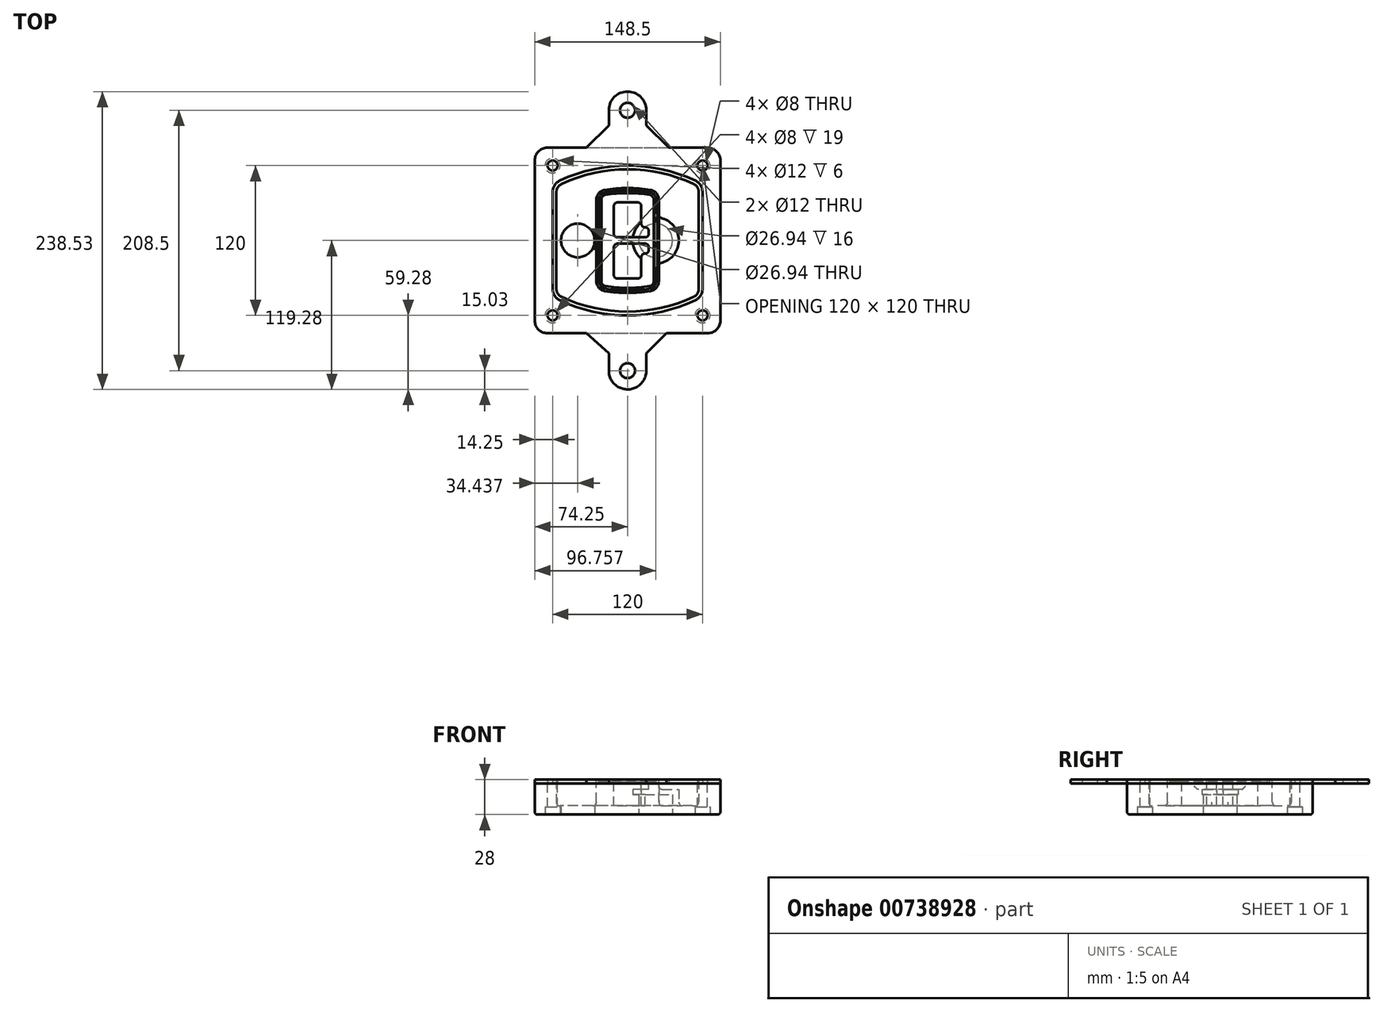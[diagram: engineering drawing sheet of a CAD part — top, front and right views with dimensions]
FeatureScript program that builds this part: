
annotation { "Feature Type Name" : "Feature", "Feature Type Description" : "" }
export const myFeature = defineFeature(function(context is Context, id is Id, definition is map)
    precondition{}
    {
        {
            var Q0;
            Q0=qCreatedBy(makeId("Top.planeOp"),FACE);
            var sketch = newSketch(context, id + "F0", { "sketchPlane" : qUnion([Q0])});
            skPoint(sketch, "E0.rect.middle", {"position": v(0, 0) * mm});
            skLineSegment(sketch, "E1.bottom", {"start": v(-64.25, -74.25) * mm, "end": v(64.25, -74.25) * mm});
            skLineSegment(sketch, "E1.top", {"start": v(-64.25, 74.25) * mm, "end": v(64.25, 74.25) * mm});
            skLineSegment(sketch, "E1.left", {"start": v(-74.25, -64.25) * mm, "end": v(-74.25, 64.25) * mm});
            skLineSegment(sketch, "E1.right", {"start": v(74.25, -64.25) * mm, "end": v(74.25, 64.25) * mm});
            skLineSegment(sketch, "E2", {"start": v(-74.25, 74.25) * mm, "end": v(74.25, -74.25) * mm, "construction": true});
            skLineSegment(sketch, "E3", {"start": v(74.25, 74.25) * mm, "end": v(-74.25, -74.25) * mm, "construction": true});
            skCircle(sketch, "E4", {"center": v(-60, 60) * mm, "radius": 4 * mm});
            skCircle(sketch, "E5", {"center": v(60, 60) * mm, "radius": 4 * mm});
            skCircle(sketch, "E6", {"center": v(60, -60) * mm, "radius": 4 * mm});
            skCircle(sketch, "E7", {"center": v(-60, -60) * mm, "radius": 4 * mm});
            skLineSegment(sketch, "E8", {"start": v(-60, 60) * mm, "end": v(60, 60) * mm, "construction": true});
            skLineSegment(sketch, "E9", {"start": v(60, 60) * mm, "end": v(60, -60) * mm, "construction": true});
            skLineSegment(sketch, "E10", {"start": v(60, -60) * mm, "end": v(-60, -60) * mm, "construction": true});
            skLineSegment(sketch, "E11", {"start": v(-60, -60) * mm, "end": v(-60, 60) * mm, "construction": true});
            skLineSegment(sketch, "E12", {"start": v(-60, 38.83) * mm, "end": v(-60, -38.83) * mm});
            skLineSegment(sketch, "E13", {"start": v(60, 38.83) * mm, "end": v(60, -38.83) * mm});
            skArc(sketch, "E14", {"start": v(54.26, 47.88) * mm, "mid": v(0, 60) * mm, "end": v(-54.26, 47.88) * mm});
            skArc(sketch, "E15", {"start": v(-54.26, -47.88) * mm, "mid": v(0, -60) * mm, "end": v(54.26, -47.88) * mm});
            skLineSegment(sketch, "E16", {"start": v(-60, 0) * mm, "end": v(60, 0) * mm, "construction": true});
            skPoint(sketch, "E17.visualSharp", {"position": v(-60, -45) * mm});
            skArc(sketch, "E17.filletArc", {"start": v(-60, -38.83) * mm, "mid": v(-58.44, -44.2) * mm, "end": v(-54.26, -47.88) * mm});
            skPoint(sketch, "E18.visualSharp", {"position": v(-60, 45) * mm});
            skArc(sketch, "E18.filletArc", {"start": v(-54.26, 47.88) * mm, "mid": v(-58.44, 44.2) * mm, "end": v(-60, 38.83) * mm});
            skPoint(sketch, "E19.visualSharp", {"position": v(60, 45) * mm});
            skArc(sketch, "E19.filletArc", {"start": v(60, 38.83) * mm, "mid": v(58.44, 44.2) * mm, "end": v(54.26, 47.88) * mm});
            skPoint(sketch, "E20.visualSharp", {"position": v(60, -45) * mm});
            skArc(sketch, "E20.filletArc", {"start": v(54.26, -47.88) * mm, "mid": v(58.44, -44.2) * mm, "end": v(60, -38.83) * mm});
            skPoint(sketch, "E21.visualSharp", {"position": v(-74.25, 74.25) * mm});
            skArc(sketch, "E21.filletArc", {"start": v(-64.25, 74.25) * mm, "mid": v(-71.32, 71.32) * mm, "end": v(-74.25, 64.25) * mm});
            skPoint(sketch, "E22.visualSharp", {"position": v(74.25, 74.25) * mm});
            skArc(sketch, "E22.filletArc", {"start": v(74.25, 64.25) * mm, "mid": v(71.32, 71.32) * mm, "end": v(64.25, 74.25) * mm});
            skPoint(sketch, "E23.visualSharp", {"position": v(74.25, -74.25) * mm});
            skArc(sketch, "E23.filletArc", {"start": v(64.25, -74.25) * mm, "mid": v(71.32, -71.32) * mm, "end": v(74.25, -64.25) * mm});
            skPoint(sketch, "E24.visualSharp", {"position": v(-74.25, -74.25) * mm});
            skArc(sketch, "E24.filletArc", {"start": v(-74.25, -64.25) * mm, "mid": v(-71.32, -71.32) * mm, "end": v(-64.25, -74.25) * mm});
            skArc(sketch, "E25.0", {"start": v(57, 38.83) * mm, "mid": v(55.9, 42.58) * mm, "end": v(52.98, 45.17) * mm});
            skLineSegment(sketch, "E25.1", {"start": v(57, 38.83) * mm, "end": v(57, -38.83) * mm});
            skArc(sketch, "E25.2", {"start": v(52.98, -45.17) * mm, "mid": v(55.9, -42.58) * mm, "end": v(57, -38.83) * mm});
            skArc(sketch, "E25.3", {"start": v(-52.98, -45.17) * mm, "mid": v(0, -57) * mm, "end": v(52.98, -45.17) * mm});
            skArc(sketch, "E25.4", {"start": v(-57, -38.83) * mm, "mid": v(-55.9, -42.58) * mm, "end": v(-52.98, -45.17) * mm});
            skArc(sketch, "E25.5", {"start": v(52.98, 45.17) * mm, "mid": v(0, 57) * mm, "end": v(-52.98, 45.17) * mm});
            skLineSegment(sketch, "E25.6", {"start": v(-57, 38.83) * mm, "end": v(-57, -38.83) * mm});
            skArc(sketch, "E25.7", {"start": v(-52.98, 45.17) * mm, "mid": v(-55.9, 42.58) * mm, "end": v(-57, 38.83) * mm});
            skArc(sketch, "E26.0", {"start": v(-55.96, 51.5) * mm, "mid": v(-61.82, 46.33) * mm, "end": v(-64, 38.83) * mm});
            skArc(sketch, "E26.1", {"start": v(55.96, 51.5) * mm, "mid": v(0, 64) * mm, "end": v(-55.96, 51.5) * mm});
            skArc(sketch, "E26.2", {"start": v(64, 38.83) * mm, "mid": v(61.82, 46.33) * mm, "end": v(55.96, 51.5) * mm});
            skLineSegment(sketch, "E26.3", {"start": v(64, 38.83) * mm, "end": v(64, -38.83) * mm});
            skArc(sketch, "E26.4", {"start": v(55.96, -51.5) * mm, "mid": v(61.82, -46.33) * mm, "end": v(64, -38.83) * mm});
            skLineSegment(sketch, "E26.5", {"start": v(-64, 38.83) * mm, "end": v(-64, -38.83) * mm});
            skArc(sketch, "E26.6", {"start": v(-55.96, -51.5) * mm, "mid": v(0, -64) * mm, "end": v(55.96, -51.5) * mm});
            skArc(sketch, "E26.7", {"start": v(-64, -38.83) * mm, "mid": v(-61.82, -46.33) * mm, "end": v(-55.96, -51.5) * mm});
            skSolve(sketch);
        }
        {
            var Q0;
            Q0=makeQuery(id+"F0.imprint","IMPRINT",FACE,{"disambiguationData":[TD([[makeQuery(id+"F0.imprint","IMPRINT",EDGE,{"derivedFrom":sQuery(id+"F0.wireOp",EDGE,"E1.bottom")}),1.0]])]});
            var Q1;
            Q1=makeQuery(id+"F0.imprint","IMPRINT",FACE,{"disambiguationData":[TD([[makeQuery(id+"F0.imprint","IMPRINT",EDGE,{"derivedFrom":sQuery(id+"F0.wireOp",EDGE,"E12")}),1.0]])]});
            var Q2;
            Q2=makeQuery(id+"F0.imprint","IMPRINT",FACE,{"disambiguationData":[TD([[makeQuery(id+"F0.imprint","IMPRINT",EDGE,{"derivedFrom":sQuery(id+"F0.wireOp",EDGE,"E25.0")}),1.0]])]});
            var Q3;
            Q3=makeQuery(id+"F0.imprint","IMPRINT",FACE,{"disambiguationData":[TD([[makeQuery(id+"F0.imprint","IMPRINT",EDGE,{"derivedFrom":sQuery(id+"F0.wireOp",EDGE,"E12")}),-1.0]])]});
            extrude(context, id + "F1", {"entities" : qUnion([Q0, Q1, Q2, Q3]), "oppositeDirection" : true, "depth" : 25 * mm, "offsetDistance" : 25 * mm});
        }
        {
            var Q0;
            Q0=makeQuery(id+"F0.imprint","IMPRINT",FACE,{"disambiguationData":[TD([[makeQuery(id+"F0.imprint","IMPRINT",EDGE,{"derivedFrom":sQuery(id+"F0.wireOp",EDGE,"E12")}),1.0]])]});
            extrude(context, id + "F2", {"entities" : qUnion([Q0]), "operationType" : NewBodyOperationType.ADD, "depth" : 3 * mm, "offsetDistance" : 25 * mm});
        }
        {
            var Q0;
            Q0=makeQuery(id+"F0.imprint","IMPRINT",FACE,{"disambiguationData":[TD([[makeQuery(id+"F0.imprint","IMPRINT",EDGE,{"derivedFrom":sQuery(id+"F0.wireOp",EDGE,"E25.0")}),1.0]])]});
            extrude(context, id + "F3", {"entities" : qUnion([Q0]), "operationType" : NewBodyOperationType.REMOVE, "oppositeDirection" : true, "depth" : 18 * mm});
        }
        {
            var Q0;
            Q0=makeQuery(id+"F2.opExtrude","CAP_FACE",FACE,{"disambiguationData":[OSD([sQuery(id+"F0.wireOp",EDGE,"E12"),sQuery(id+"F0.wireOp",EDGE,"E13"),sQuery(id+"F0.wireOp",EDGE,"E14"),sQuery(id+"F0.wireOp",EDGE,"E15"),sQuery(id+"F0.wireOp",EDGE,"E17.filletArc"),sQuery(id+"F0.wireOp",EDGE,"E18.filletArc"),sQuery(id+"F0.wireOp",EDGE,"E19.filletArc"),sQuery(id+"F0.wireOp",EDGE,"E20.filletArc"),sQuery(id+"F0.wireOp",EDGE,"E25.0"),sQuery(id+"F0.wireOp",EDGE,"E25.1"),sQuery(id+"F0.wireOp",EDGE,"E25.2"),sQuery(id+"F0.wireOp",EDGE,"E25.3"),sQuery(id+"F0.wireOp",EDGE,"E25.4"),sQuery(id+"F0.wireOp",EDGE,"E25.5"),sQuery(id+"F0.wireOp",EDGE,"E25.6"),sQuery(id+"F0.wireOp",EDGE,"E25.7")])],"isStart":false});
            var sketch = newSketch(context, id + "F4", { "sketchPlane" : qUnion([Q0])});
            skArc(sketch, "E27.0", {"start": v(-18.34, -40.45) * mm, "mid": v(0, -42) * mm, "end": v(18.34, -40.45) * mm});
            skArc(sketch, "E28.0", {"start": v(18.34, 40.45) * mm, "mid": v(0, 42) * mm, "end": v(-18.34, 40.45) * mm});
            skLineSegment(sketch, "E29", {"start": v(-25, 32.57) * mm, "end": v(-25, -32.57) * mm});
            skLineSegment(sketch, "E30", {"start": v(25, 32.57) * mm, "end": v(25, -32.57) * mm});
            skLineSegment(sketch, "E31", {"start": v(-25, 39.1) * mm, "end": v(25, 39.1) * mm, "construction": true});
            skLineSegment(sketch, "E32", {"start": v(-25, -39.1) * mm, "end": v(25, -39.1) * mm, "construction": true});
            skPoint(sketch, "E33.visualSharp", {"position": v(-25, 39.1) * mm});
            skArc(sketch, "E33.filletArc", {"start": v(-18.34, 40.45) * mm, "mid": v(-23.11, 37.73) * mm, "end": v(-25, 32.57) * mm});
            skPoint(sketch, "E34.visualSharp", {"position": v(25, 39.1) * mm});
            skArc(sketch, "E34.filletArc", {"start": v(25, 32.57) * mm, "mid": v(23.11, 37.73) * mm, "end": v(18.34, 40.45) * mm});
            skPoint(sketch, "E35.visualSharp", {"position": v(25, -39.1) * mm});
            skArc(sketch, "E35.filletArc", {"start": v(18.34, -40.45) * mm, "mid": v(23.11, -37.73) * mm, "end": v(25, -32.57) * mm});
            skPoint(sketch, "E36.visualSharp", {"position": v(-25, -39.1) * mm});
            skArc(sketch, "E36.filletArc", {"start": v(-25, -32.57) * mm, "mid": v(-23.11, -37.73) * mm, "end": v(-18.34, -40.45) * mm});
            skArc(sketch, "E37.0", {"start": v(52.98, 45.17) * mm, "mid": v(0, 57) * mm, "end": v(-52.98, 45.17) * mm});
            skArc(sketch, "E37.1", {"start": v(-52.98, 45.17) * mm, "mid": v(-55.9, 42.58) * mm, "end": v(-57, 38.83) * mm});
            skLineSegment(sketch, "E37.2", {"start": v(-57, 38.83) * mm, "end": v(-57, -38.83) * mm});
            skArc(sketch, "E37.3", {"start": v(-57, -38.83) * mm, "mid": v(-55.9, -42.58) * mm, "end": v(-52.98, -45.17) * mm});
            skArc(sketch, "E37.4", {"start": v(-52.98, -45.17) * mm, "mid": v(0, -57) * mm, "end": v(52.98, -45.17) * mm});
            skArc(sketch, "E37.5", {"start": v(52.98, -45.17) * mm, "mid": v(55.9, -42.58) * mm, "end": v(57, -38.83) * mm});
            skLineSegment(sketch, "E37.6", {"start": v(57, 38.83) * mm, "end": v(57, -38.83) * mm});
            skArc(sketch, "E37.7", {"start": v(57, 38.83) * mm, "mid": v(55.9, 42.58) * mm, "end": v(52.98, 45.17) * mm});
            skLineSegment(sketch, "E38.0", {"start": v(23, 32.57) * mm, "end": v(23, -32.57) * mm});
            skArc(sketch, "E38.1", {"start": v(18, -38.48) * mm, "mid": v(21.58, -36.44) * mm, "end": v(23, -32.57) * mm});
            skArc(sketch, "E38.2", {"start": v(-18, -38.48) * mm, "mid": v(0, -40) * mm, "end": v(18, -38.48) * mm});
            skArc(sketch, "E38.3", {"start": v(-23, -32.57) * mm, "mid": v(-21.58, -36.44) * mm, "end": v(-18, -38.48) * mm});
            skLineSegment(sketch, "E38.4", {"start": v(-23, 32.57) * mm, "end": v(-23, -32.57) * mm});
            skArc(sketch, "E38.5", {"start": v(23, 32.57) * mm, "mid": v(21.58, 36.44) * mm, "end": v(18, 38.48) * mm});
            skArc(sketch, "E38.6", {"start": v(-18, 38.48) * mm, "mid": v(-21.58, 36.44) * mm, "end": v(-23, 32.57) * mm});
            skArc(sketch, "E38.7", {"start": v(18, 38.48) * mm, "mid": v(0, 40) * mm, "end": v(-18, 38.48) * mm});
            skArc(sketch, "E39.0", {"start": v(21, 32.57) * mm, "mid": v(20.06, 35.15) * mm, "end": v(17.67, 36.5) * mm});
            skLineSegment(sketch, "E39.1", {"start": v(21, 32.57) * mm, "end": v(21, -32.57) * mm});
            skArc(sketch, "E39.2", {"start": v(17.67, -36.5) * mm, "mid": v(20.06, -35.15) * mm, "end": v(21, -32.57) * mm});
            skArc(sketch, "E39.3", {"start": v(-17.67, -36.5) * mm, "mid": v(0, -38) * mm, "end": v(17.67, -36.5) * mm});
            skArc(sketch, "E39.4", {"start": v(-21, -32.57) * mm, "mid": v(-20.06, -35.15) * mm, "end": v(-17.67, -36.5) * mm});
            skArc(sketch, "E39.5", {"start": v(17.67, 36.5) * mm, "mid": v(0, 38) * mm, "end": v(-17.67, 36.5) * mm});
            skLineSegment(sketch, "E39.6", {"start": v(-21, 32.57) * mm, "end": v(-21, -32.57) * mm});
            skArc(sketch, "E39.7", {"start": v(-17.67, 36.5) * mm, "mid": v(-20.06, 35.15) * mm, "end": v(-21, 32.57) * mm});
            skLineSegment(sketch, "E40", {"start": v(-25, 0) * mm, "end": v(25, 0) * mm, "construction": true});
            skLineSegment(sketch, "E41", {"start": v(-11, 5.5) * mm, "end": v(-11, 27.5) * mm});
            skLineSegment(sketch, "E42", {"start": v(-8, 30.5) * mm, "end": v(8, 30.5) * mm});
            skLineSegment(sketch, "E43", {"start": v(11, 27.5) * mm, "end": v(11, 13.5) * mm});
            skLineSegment(sketch, "E44", {"start": v(14, 10.5) * mm, "end": v(14, 10.5) * mm});
            skLineSegment(sketch, "E45", {"start": v(17, 7.5) * mm, "end": v(17, 5.5) * mm});
            skLineSegment(sketch, "E46", {"start": v(14, 2.5) * mm, "end": v(-8, 2.5) * mm});
            skPoint(sketch, "E47.visualSharp", {"position": v(-11, 30.5) * mm});
            skArc(sketch, "E47.filletArc", {"start": v(-8, 30.5) * mm, "mid": v(-10.12, 29.62) * mm, "end": v(-11, 27.5) * mm});
            skPoint(sketch, "E48.visualSharp", {"position": v(11, 30.5) * mm});
            skArc(sketch, "E48.filletArc", {"start": v(11, 27.5) * mm, "mid": v(10.12, 29.62) * mm, "end": v(8, 30.5) * mm});
            skPoint(sketch, "E49.visualSharp", {"position": v(11, 10.5) * mm});
            skArc(sketch, "E49.filletArc", {"start": v(11, 13.5) * mm, "mid": v(11.88, 11.38) * mm, "end": v(14, 10.5) * mm});
            skPoint(sketch, "E50.visualSharp", {"position": v(17, 10.5) * mm});
            skArc(sketch, "E50.filletArc", {"start": v(17, 7.5) * mm, "mid": v(16.12, 9.62) * mm, "end": v(14, 10.5) * mm});
            skPoint(sketch, "E51.visualSharp", {"position": v(17, 2.5) * mm});
            skArc(sketch, "E51.filletArc", {"start": v(14, 2.5) * mm, "mid": v(16.12, 3.38) * mm, "end": v(17, 5.5) * mm});
            skPoint(sketch, "E52.visualSharp", {"position": v(-11, 2.5) * mm});
            skArc(sketch, "E52.filletArc", {"start": v(-11, 5.5) * mm, "mid": v(-10.12, 3.38) * mm, "end": v(-8, 2.5) * mm});
            skLineSegment(sketch, "E53.0.MirrorCS", {"start": v(14, -2.5) * mm, "end": v(-8, -2.5) * mm});
            skArc(sketch, "E54.0.MirrorCS", {"start": v(-11, -5.5) * mm, "mid": v(-10.12, -3.38) * mm, "end": v(-8, -2.5) * mm});
            skLineSegment(sketch, "E55.0.MirrorCS", {"start": v(-11, -5.5) * mm, "end": v(-11, -27.5) * mm});
            skArc(sketch, "E56.0.MirrorCS", {"start": v(-8, -30.5) * mm, "mid": v(-10.12, -29.62) * mm, "end": v(-11, -27.5) * mm});
            skLineSegment(sketch, "E57.0.MirrorCS", {"start": v(-8, -30.5) * mm, "end": v(8, -30.5) * mm});
            skArc(sketch, "E58.0.MirrorCS", {"start": v(11, -27.5) * mm, "mid": v(10.12, -29.62) * mm, "end": v(8, -30.5) * mm});
            skLineSegment(sketch, "E59.0.MirrorCS", {"start": v(11, -27.5) * mm, "end": v(11, -13.5) * mm});
            skArc(sketch, "E60.0.MirrorCS", {"start": v(11, -13.5) * mm, "mid": v(11.88, -11.38) * mm, "end": v(14, -10.5) * mm});
            skArc(sketch, "E61.0.MirrorCS", {"start": v(17, -7.5) * mm, "mid": v(16.12, -9.62) * mm, "end": v(14, -10.5) * mm});
            skLineSegment(sketch, "E62.0.MirrorCS", {"start": v(17, -7.5) * mm, "end": v(17, -5.5) * mm});
            skArc(sketch, "E63.0.MirrorCS", {"start": v(14, -2.5) * mm, "mid": v(16.12, -3.38) * mm, "end": v(17, -5.5) * mm});
            skSolve(sketch);
        }
        {
            var Q0;
            Q0=makeQuery(id+"F4.imprint","IMPRINT",FACE,{"disambiguationData":[TD([[makeQuery(id+"F4.imprint","IMPRINT",EDGE,{"derivedFrom":sQuery(id+"F4.wireOp",EDGE,"E27.0")}),1.0]])]});
            var Q1;
            Q1=makeQuery(id+"F4.imprint","IMPRINT",FACE,{"disambiguationData":[TD([[makeQuery(id+"F4.imprint","IMPRINT",EDGE,{"derivedFrom":sQuery(id+"F4.wireOp",EDGE,"E38.0")}),-1.0]])]});
            var Q2;
            Q2=makeQuery(id+"F4.imprint","IMPRINT",FACE,{"disambiguationData":[TD([[makeQuery(id+"F4.imprint","IMPRINT",EDGE,{"derivedFrom":sQuery(id+"F4.wireOp",EDGE,"E39.0")}),1.0]])]});
            extrude(context, id + "F5", {"entities" : qUnion([Q0, Q1, Q2]), "operationType" : NewBodyOperationType.ADD, "endBound" : BoundingType.UP_TO_NEXT, "oppositeDirection" : true, "depth" : 25 * mm});
        }
        {
            var Q0;
            Q0=makeQuery(id+"F4.imprint","IMPRINT",FACE,{"disambiguationData":[TD([[makeQuery(id+"F4.imprint","IMPRINT",EDGE,{"derivedFrom":sQuery(id+"F4.wireOp",EDGE,"E38.0")}),-1.0]])]});
            extrude(context, id + "F6", {"entities" : qUnion([Q0]), "operationType" : NewBodyOperationType.REMOVE, "oppositeDirection" : true, "depth" : 2 * mm});
        }
        {
            var Q0;
            Q0=makeQuery(id+"F1.opExtrude","CAP_FACE",FACE,{"disambiguationData":[OSD([sQuery(id+"F0.wireOp",EDGE,"E1.bottom"),sQuery(id+"F0.wireOp",EDGE,"E1.top"),sQuery(id+"F0.wireOp",EDGE,"E1.left"),sQuery(id+"F0.wireOp",EDGE,"E1.right"),sQuery(id+"F0.wireOp",EDGE,"E4"),sQuery(id+"F0.wireOp",EDGE,"E5"),sQuery(id+"F0.wireOp",EDGE,"E6"),sQuery(id+"F0.wireOp",EDGE,"E7"),sQuery(id+"F0.wireOp",EDGE,"E21.filletArc"),sQuery(id+"F0.wireOp",EDGE,"E22.filletArc"),sQuery(id+"F0.wireOp",EDGE,"E23.filletArc"),sQuery(id+"F0.wireOp",EDGE,"E24.filletArc")])],"isStart":false});
            var sketch = newSketch(context, id + "F7", { "sketchPlane" : qUnion([Q0])});
            skCircle(sketch, "E64", {"center": v(22.5, 0) * mm, "radius": 13.47 * mm});
            skCircle(sketch, "E65", {"center": v(-39.81, 0) * mm, "radius": 13.47 * mm});
            skLineSegment(sketch, "E66", {"start": v(74.25, 0) * mm, "end": v(-74.25, 0) * mm});
            skCircle(sketch, "E67", {"center": v(22.5, 0) * mm, "radius": 18.47 * mm});
            skCircle(sketch, "E68", {"center": v(60, -60) * mm, "radius": 6 * mm});
            skCircle(sketch, "E69", {"center": v(-60, -60) * mm, "radius": 6 * mm});
            skCircle(sketch, "E70", {"center": v(-60, 60) * mm, "radius": 6 * mm});
            skCircle(sketch, "E71", {"center": v(60, 60) * mm, "radius": 6 * mm});
            skSolve(sketch);
        }
        {
            var Q0;
            {var subQ1=sQuery(id+"F7.wireOp",EDGE,"E66");var subQ4=sQuery(id+"F7.wireOp",EDGE,"E64");var subQ6=makeQuery(id+"F7.imprint","INTERSECT",VERTEX,{"disambiguationData":[OD(0.0)],"derivedFrom":[subQ4,subQ1]});Q0=makeQuery(id+"F7.imprint","IMPRINT",FACE,{"disambiguationData":[TD([[makeQuery(id+"F7.imprint","IMPRINT",EDGE,{"disambiguationData":[TD([[subQ6,-1.0]])],"derivedFrom":subQ4}),-1.0]])]});}
            var Q1;
            {var subQ0=sQuery(id+"F7.wireOp",EDGE,"E66");var subQ1=sQuery(id+"F7.wireOp",EDGE,"E64");var subQ3=makeQuery(id+"F7.imprint","INTERSECT",VERTEX,{"disambiguationData":[OD(0.0)],"derivedFrom":[subQ1,subQ0]});Q1=makeQuery(id+"F7.imprint","IMPRINT",FACE,{"disambiguationData":[TD([[makeQuery(id+"F7.imprint","IMPRINT",EDGE,{"disambiguationData":[TD([[subQ3,-1.0]])],"derivedFrom":subQ1}),1.0]])]});}
            var Q2;
            {var subQ0=sQuery(id+"F7.wireOp",EDGE,"E66");var subQ1=sQuery(id+"F7.wireOp",EDGE,"E64");var subQ3=makeQuery(id+"F7.imprint","INTERSECT",VERTEX,{"disambiguationData":[OD(0.0)],"derivedFrom":[subQ1,subQ0]});Q2=makeQuery(id+"F7.imprint","IMPRINT",FACE,{"disambiguationData":[TD([[makeQuery(id+"F7.imprint","IMPRINT",EDGE,{"disambiguationData":[TD([[subQ3,1.0]])],"derivedFrom":subQ1}),1.0]])]});}
            var Q3;
            {var subQ1=sQuery(id+"F7.wireOp",EDGE,"E66");var subQ4=sQuery(id+"F7.wireOp",EDGE,"E64");var subQ6=makeQuery(id+"F7.imprint","INTERSECT",VERTEX,{"disambiguationData":[OD(0.0)],"derivedFrom":[subQ4,subQ1]});Q3=makeQuery(id+"F7.imprint","IMPRINT",FACE,{"disambiguationData":[TD([[makeQuery(id+"F7.imprint","IMPRINT",EDGE,{"disambiguationData":[TD([[subQ6,1.0]])],"derivedFrom":subQ4}),-1.0]])]});}
            extrude(context, id + "F8", {"entities" : qUnion([Q0, Q1, Q2, Q3]), "operationType" : NewBodyOperationType.ADD, "oppositeDirection" : true, "depth" : 20 * mm});
        }
        {
            var Q0;
            {var subQ0=sQuery(id+"F7.wireOp",EDGE,"E66");var subQ1=sQuery(id+"F7.wireOp",EDGE,"E64");var subQ3=makeQuery(id+"F7.imprint","INTERSECT",VERTEX,{"disambiguationData":[OD(0.0)],"derivedFrom":[subQ1,subQ0]});Q0=makeQuery(id+"F7.imprint","IMPRINT",FACE,{"disambiguationData":[TD([[makeQuery(id+"F7.imprint","IMPRINT",EDGE,{"disambiguationData":[TD([[subQ3,-1.0]])],"derivedFrom":subQ1}),1.0]])]});}
            var Q1;
            {var subQ0=sQuery(id+"F7.wireOp",EDGE,"E66");var subQ1=sQuery(id+"F7.wireOp",EDGE,"E64");var subQ3=makeQuery(id+"F7.imprint","INTERSECT",VERTEX,{"disambiguationData":[OD(0.0)],"derivedFrom":[subQ1,subQ0]});Q1=makeQuery(id+"F7.imprint","IMPRINT",FACE,{"disambiguationData":[TD([[makeQuery(id+"F7.imprint","IMPRINT",EDGE,{"disambiguationData":[TD([[subQ3,1.0]])],"derivedFrom":subQ1}),1.0]])]});}
            extrude(context, id + "F9", {"entities" : qUnion([Q0, Q1]), "operationType" : NewBodyOperationType.REMOVE, "oppositeDirection" : true, "depth" : 16 * mm});
        }
        {
            var Q0;
            {var subQ0=sQuery(id+"F7.wireOp",EDGE,"E66");var subQ1=sQuery(id+"F7.wireOp",EDGE,"E65");var subQ3=makeQuery(id+"F7.imprint","INTERSECT",VERTEX,{"disambiguationData":[OD(0.0)],"derivedFrom":[subQ1,subQ0]});Q0=makeQuery(id+"F7.imprint","IMPRINT",FACE,{"disambiguationData":[TD([[makeQuery(id+"F7.imprint","IMPRINT",EDGE,{"disambiguationData":[TD([[subQ3,-1.0]])],"derivedFrom":subQ1}),1.0]])]});}
            var Q1;
            {var subQ0=sQuery(id+"F7.wireOp",EDGE,"E66");var subQ1=sQuery(id+"F7.wireOp",EDGE,"E65");var subQ3=makeQuery(id+"F7.imprint","INTERSECT",VERTEX,{"disambiguationData":[OD(0.0)],"derivedFrom":[subQ1,subQ0]});Q1=makeQuery(id+"F7.imprint","IMPRINT",FACE,{"disambiguationData":[TD([[makeQuery(id+"F7.imprint","IMPRINT",EDGE,{"disambiguationData":[TD([[subQ3,1.0]])],"derivedFrom":subQ1}),1.0]])]});}
            extrude(context, id + "F10", {"entities" : qUnion([Q0, Q1]), "operationType" : NewBodyOperationType.REMOVE, "oppositeDirection" : true, "depth" : 25 * mm});
        }
        {
            var Q0;
            Q0=makeQuery(id+"F7.imprint","IMPRINT",FACE,{"disambiguationData":[TD([[makeQuery(id+"F7.imprint","IMPRINT",EDGE,{"derivedFrom":sQuery(id+"F7.wireOp",EDGE,"E68")}),1.0]])]});
            var Q1;
            Q1=makeQuery(id+"F7.imprint","IMPRINT",FACE,{"disambiguationData":[TD([[makeQuery(id+"F7.imprint","IMPRINT",EDGE,{"derivedFrom":makeQuery(id+"F1.opExtrude","CAP_EDGE",EDGE,{"disambiguationData":[OSD([sQuery(id+"F0.wireOp",EDGE,"E5")])],"isStart":false})}),-1.0]])]});
            var Q2;
            Q2=makeQuery(id+"F7.imprint","IMPRINT",FACE,{"disambiguationData":[TD([[makeQuery(id+"F7.imprint","IMPRINT",EDGE,{"derivedFrom":sQuery(id+"F7.wireOp",EDGE,"E69")}),1.0]])]});
            var Q3;
            Q3=makeQuery(id+"F7.imprint","IMPRINT",FACE,{"disambiguationData":[TD([[makeQuery(id+"F7.imprint","IMPRINT",EDGE,{"derivedFrom":makeQuery(id+"F1.opExtrude","CAP_EDGE",EDGE,{"disambiguationData":[OSD([sQuery(id+"F0.wireOp",EDGE,"E4")])],"isStart":false})}),-1.0]])]});
            var Q4;
            Q4=makeQuery(id+"F7.imprint","IMPRINT",FACE,{"disambiguationData":[TD([[makeQuery(id+"F7.imprint","IMPRINT",EDGE,{"derivedFrom":sQuery(id+"F7.wireOp",EDGE,"E70")}),1.0]])]});
            var Q5;
            Q5=makeQuery(id+"F7.imprint","IMPRINT",FACE,{"disambiguationData":[TD([[makeQuery(id+"F7.imprint","IMPRINT",EDGE,{"derivedFrom":makeQuery(id+"F1.opExtrude","CAP_EDGE",EDGE,{"disambiguationData":[OSD([sQuery(id+"F0.wireOp",EDGE,"E7")])],"isStart":false})}),-1.0]])]});
            var Q6;
            Q6=makeQuery(id+"F7.imprint","IMPRINT",FACE,{"disambiguationData":[TD([[makeQuery(id+"F7.imprint","IMPRINT",EDGE,{"derivedFrom":sQuery(id+"F7.wireOp",EDGE,"E71")}),1.0]])]});
            var Q7;
            Q7=makeQuery(id+"F7.imprint","IMPRINT",FACE,{"disambiguationData":[TD([[makeQuery(id+"F7.imprint","IMPRINT",EDGE,{"derivedFrom":makeQuery(id+"F1.opExtrude","CAP_EDGE",EDGE,{"disambiguationData":[OSD([sQuery(id+"F0.wireOp",EDGE,"E6")])],"isStart":false})}),-1.0]])]});
            extrude(context, id + "F11", {"entities" : qUnion([Q0, Q1, Q2, Q3, Q4, Q5, Q6, Q7]), "operationType" : NewBodyOperationType.REMOVE, "oppositeDirection" : true, "depth" : 6 * mm});
        }
        {
            var Q0;
            Q0=makeQuery(id+"F9.boolean.opBoolean","COPY",FACE,{"derivedFrom":makeQuery(id+"F9.opExtrude","CAP_FACE",FACE,{"disambiguationData":[OSD([sQuery(id+"F7.wireOp",EDGE,"E64")])],"isStart":false})});
            var sketch = newSketch(context, id + "F12", { "sketchPlane" : qUnion([Q0])});
            skArc(sketch, "E72.0", {"start": v(11, 14.45) * mm, "mid": v(6.45, 9.13) * mm, "end": v(4.2, 2.5) * mm});
            skArc(sketch, "E72.1", {"start": v(4.2, -2.5) * mm, "mid": v(6.45, -9.13) * mm, "end": v(11, -14.45) * mm});
            skLineSegment(sketch, "E73", {"start": v(4.2, -2.5) * mm, "end": v(14, -2.5) * mm});
            skLineSegment(sketch, "E74.0", {"start": v(14, 2.5) * mm, "end": v(4.2, 2.5) * mm});
            skArc(sketch, "E74.1", {"start": v(14, 2.5) * mm, "mid": v(16.12, 3.38) * mm, "end": v(17, 5.5) * mm});
            skLineSegment(sketch, "E74.2", {"start": v(17, 7.5) * mm, "end": v(17, 5.5) * mm});
            skArc(sketch, "E74.3", {"start": v(17, 7.5) * mm, "mid": v(16.12, 9.62) * mm, "end": v(14, 10.5) * mm});
            skArc(sketch, "E74.4", {"start": v(11, 13.5) * mm, "mid": v(11.88, 11.38) * mm, "end": v(14, 10.5) * mm});
            skLineSegment(sketch, "E74.5", {"start": v(11, 14.45) * mm, "end": v(11, 13.5) * mm});
            skLineSegment(sketch, "E74.7", {"start": v(14, -2.5) * mm, "end": v(4.2, -2.5) * mm});
            skArc(sketch, "E74.8", {"start": v(14, -2.5) * mm, "mid": v(16.12, -3.38) * mm, "end": v(17, -5.5) * mm});
            skLineSegment(sketch, "E74.9", {"start": v(17, -7.5) * mm, "end": v(17, -5.5) * mm});
            skArc(sketch, "E74.10", {"start": v(17, -7.5) * mm, "mid": v(16.12, -9.62) * mm, "end": v(14, -10.5) * mm});
            skArc(sketch, "E74.11", {"start": v(11, -13.5) * mm, "mid": v(11.88, -11.38) * mm, "end": v(14, -10.5) * mm});
            skLineSegment(sketch, "E74.12", {"start": v(11, -14.45) * mm, "end": v(11, -13.5) * mm});
            skPoint(sketch, "E75.orphan", {"position": v(11, -27.5) * mm});
            skPoint(sketch, "E76.orphan", {"position": v(-8, -2.5) * mm});
            skPoint(sketch, "E77.orphan", {"position": v(-8, 2.5) * mm});
            skPoint(sketch, "E78.orphan", {"position": v(11, 27.5) * mm});
            skSolve(sketch);
        }
        {
            var Q0;
            {var subQ7=sQuery(id+"F12.wireOp",EDGE,"E72.0");var subQ14=sQuery(id+"F12.wireOp",EDGE,"E72.1");var subQ16=sQuery(id+"F12.wireOp",EDGE,"E74.1");var subQ18=sQuery(id+"F12.wireOp",EDGE,"E74.8");Q0=qUnion([makeQuery(id+"F12.imprint","IMPRINT",FACE,{"disambiguationData":[TD([[makeQuery(id+"F12.imprint","IMPRINT",EDGE,{"derivedFrom":subQ7}),1.0]])]}),makeQuery(id+"F12.imprint","IMPRINT",FACE,{"disambiguationData":[TD([[makeQuery(id+"F12.imprint","IMPRINT",EDGE,{"derivedFrom":subQ14}),1.0]])]}),makeQuery(id+"F12.imprint","IMPRINT",FACE,{"disambiguationData":[TD([[makeQuery(id+"F12.imprint","IMPRINT",EDGE,{"derivedFrom":subQ16}),1.0]])]}),makeQuery(id+"F12.imprint","IMPRINT",FACE,{"disambiguationData":[TD([[makeQuery(id+"F12.imprint","IMPRINT",EDGE,{"derivedFrom":subQ18}),-1.0]])]})]);}
            var Q1;
            Q1=makeQuery(id+"F5.boolean.opBoolean","SPLIT",FACE,{"disambiguationData":[TD([makeQuery(id+"F5.opExtrude","SWEPT_FACE",FACE,{"disambiguationData":[OSD([sQuery(id+"F4.wireOp",EDGE,"E41")])]})])],"derivedFrom":makeQuery(id+"F3.boolean.opBoolean","COPY",FACE,{"derivedFrom":makeQuery(id+"F3.opExtrude","CAP_FACE",FACE,{"disambiguationData":[OSD([sQuery(id+"F0.wireOp",EDGE,"E25.0"),sQuery(id+"F0.wireOp",EDGE,"E25.1"),sQuery(id+"F0.wireOp",EDGE,"E25.2"),sQuery(id+"F0.wireOp",EDGE,"E25.3"),sQuery(id+"F0.wireOp",EDGE,"E25.4"),sQuery(id+"F0.wireOp",EDGE,"E25.5"),sQuery(id+"F0.wireOp",EDGE,"E25.6"),sQuery(id+"F0.wireOp",EDGE,"E25.7")])],"isStart":false})})});
            extrude(context, id + "F13", {"entities" : qUnion([Q0]), "operationType" : NewBodyOperationType.REMOVE, "endBound" : BoundingType.UP_TO_SURFACE, "endBoundEntityFace" : qUnion([Q1]), "depth" : 25 * mm});
        }
        {
            var Q0;
            Q0=makeQuery(id+"F3.boolean.opBoolean","COPY",EDGE,{"derivedFrom":makeQuery(id+"F3.opExtrude","CAP_EDGE",EDGE,{"disambiguationData":[OSD([sQuery(id+"F0.wireOp",EDGE,"E25.6")])],"isStart":false})});
            var Q1;
            Q1=makeQuery(id+"F8.boolean.opBoolean","INTERSECT",EDGE,{"derivedFrom":[makeQuery(id+"F5.opExtrude","SWEPT_FACE",FACE,{"disambiguationData":[OSD([sQuery(id+"F4.wireOp",EDGE,"E30")])]}),makeQuery(id+"F8.opExtrude","CAP_FACE",FACE,{"disambiguationData":[OSD([sQuery(id+"F7.wireOp",EDGE,"E67")])],"isStart":false})]});
            var Q2;
            Q2=makeQuery(id+"F8.boolean.opBoolean","INTERSECT",EDGE,{"disambiguationData":[OD(1.0)],"derivedFrom":[makeQuery(id+"F5.opExtrude","SWEPT_FACE",FACE,{"disambiguationData":[OSD([sQuery(id+"F4.wireOp",EDGE,"E30")])]}),makeQuery(id+"F8.opExtrude","SWEPT_FACE",FACE,{"disambiguationData":[OSD([sQuery(id+"F7.wireOp",EDGE,"E67")])]})]});
            var Q3;
            {var subQ0=sQuery(id+"F4.wireOp",EDGE,"E30");Q3=makeQuery(id+"F8.boolean.opBoolean","SPLIT",EDGE,{"disambiguationData":[TD([makeQuery(id+"F5.opExtrude","SWEPT_FACE",FACE,{"disambiguationData":[OSD([sQuery(id+"F4.wireOp",EDGE,"E35.filletArc")])]})])],"derivedFrom":makeQuery(id+"F5.opExtrude","CAP_EDGE",EDGE,{"disambiguationData":[OSD([subQ0])],"isStart":false})});}
            var Q4;
            {var subQ0=sQuery(id+"F0.wireOp",EDGE,"E25.7");var subQ1=sQuery(id+"F0.wireOp",EDGE,"E25.1");var subQ2=sQuery(id+"F0.wireOp",EDGE,"E25.6");var subQ3=sQuery(id+"F0.wireOp",EDGE,"E25.5");var subQ4=sQuery(id+"F0.wireOp",EDGE,"E25.4");var subQ5=sQuery(id+"F0.wireOp",EDGE,"E25.0");var subQ6=sQuery(id+"F0.wireOp",EDGE,"E25.2");var subQ7=sQuery(id+"F0.wireOp",EDGE,"E25.3");Q4=makeQuery(id+"F8.boolean.opBoolean","INTERSECT",EDGE,{"derivedFrom":[makeQuery(id+"F5.boolean.opBoolean","SPLIT",FACE,{"disambiguationData":[TD([makeQuery(id+"F2.opExtrude","SWEPT_FACE",FACE,{"disambiguationData":[OSD([subQ5])]})])],"derivedFrom":makeQuery(id+"F3.boolean.opBoolean","COPY",FACE,{"derivedFrom":makeQuery(id+"F3.opExtrude","CAP_FACE",FACE,{"disambiguationData":[OSD([subQ5,subQ1,subQ6,subQ7,subQ4,subQ3,subQ2,subQ0])],"isStart":false})})}),makeQuery(id+"F8.opExtrude","SWEPT_FACE",FACE,{"disambiguationData":[OSD([sQuery(id+"F7.wireOp",EDGE,"E67")])]})]});}
            var Q5;
            Q5=makeQuery(id+"F8.boolean.opBoolean","INTERSECT",EDGE,{"disambiguationData":[OD(0.0)],"derivedFrom":[makeQuery(id+"F5.opExtrude","SWEPT_FACE",FACE,{"disambiguationData":[OSD([sQuery(id+"F4.wireOp",EDGE,"E30")])]}),makeQuery(id+"F8.opExtrude","SWEPT_FACE",FACE,{"disambiguationData":[OSD([sQuery(id+"F7.wireOp",EDGE,"E67")])]})]});
            fillet(context, id + "F14", {"entities" : qUnion([Q0, Q1, Q2, Q3, Q4, Q5]), "radius" : 3 * mm, "tangentPropagation" : true, "allowEdgeOverflow" : false});
        }
        {
            var Q0;
            Q0=makeQuery(id+"F1.opExtrude","CAP_EDGE",EDGE,{"disambiguationData":[OSD([sQuery(id+"F0.wireOp",EDGE,"E1.bottom")])],"isStart":false});
            fillet(context, id + "F15", {"entities" : qUnion([Q0]), "radius" : 2 * mm, "tangentPropagation" : true, "allowEdgeOverflow" : false});
        }
        {
            var Q0;
            {var subQ0=sQuery(id+"F0.wireOp",EDGE,"E21.filletArc");var subQ1=sQuery(id+"F0.wireOp",EDGE,"E7");var subQ2=sQuery(id+"F0.wireOp",EDGE,"E6");var subQ3=sQuery(id+"F0.wireOp",EDGE,"E5");var subQ4=sQuery(id+"F0.wireOp",EDGE,"E4");var subQ5=sQuery(id+"F0.wireOp",EDGE,"E22.filletArc");var subQ6=sQuery(id+"F0.wireOp",EDGE,"E1.bottom");var subQ7=sQuery(id+"F0.wireOp",EDGE,"E1.right");var subQ8=sQuery(id+"F0.wireOp",EDGE,"E1.top");var subQ9=sQuery(id+"F0.wireOp",EDGE,"E1.left");var subQ10=sQuery(id+"F0.wireOp",EDGE,"E23.filletArc");var subQ11=sQuery(id+"F0.wireOp",EDGE,"E24.filletArc");Q0=makeQuery(id+"F2.boolean.opBoolean","SPLIT",FACE,{"disambiguationData":[TD([makeQuery(id+"F1.opExtrude","SWEPT_FACE",FACE,{"disambiguationData":[OSD([subQ6])]})])],"derivedFrom":makeQuery(id+"F1.opExtrude","CAP_FACE",FACE,{"disambiguationData":[OSD([subQ6,subQ8,subQ9,subQ7,subQ4,subQ3,subQ2,subQ1,subQ0,subQ5,subQ10,subQ11])],"isStart":true})});}
            var sketch = newSketch(context, id + "F16", { "sketchPlane" : qUnion([Q0])});
            skLineSegment(sketch, "E79", {"start": v(-33, 74.25) * mm, "end": v(-15, 92.25) * mm});
            skLineSegment(sketch, "E80", {"start": v(33, 74.25) * mm, "end": v(15, 92.25) * mm});
            skCircle(sketch, "E81", {"center": v(0, 104.25) * mm, "radius": 6 * mm});
            skLineSegment(sketch, "E82", {"start": v(0, 74.25) * mm, "end": v(0, 104.25) * mm, "construction": true});
            skLineSegment(sketch, "E83", {"start": v(-15, 92.25) * mm, "end": v(-15, 104.25) * mm});
            skLineSegment(sketch, "E84", {"start": v(0, -74.25) * mm, "end": v(0, -104.25) * mm, "construction": true});
            skLineSegment(sketch, "E85", {"start": v(-32.98, -74.25) * mm, "end": v(-15, -90.4) * mm});
            skLineSegment(sketch, "E86", {"start": v(-15, -90.4) * mm, "end": v(-15, -104.25) * mm});
            skLineSegment(sketch, "E87", {"start": v(31.15, -74.25) * mm, "end": v(15, -90.4) * mm});
            skLineSegment(sketch, "E88", {"start": v(15, -90.4) * mm, "end": v(15, -104.28) * mm});
            skCircle(sketch, "E89", {"center": v(0, -104.25) * mm, "radius": 6 * mm});
            skArc(sketch, "E90", {"start": v(-15, -104.25) * mm, "mid": v(-0.02, -119.28) * mm, "end": v(15, -104.28) * mm});
            skLineSegment(sketch, "E91", {"start": v(15, 92.25) * mm, "end": v(15, 104.25) * mm});
            skArc(sketch, "E92", {"start": v(15, 104.25) * mm, "mid": v(0, 119.25) * mm, "end": v(-15, 104.25) * mm});
            skSolve(sketch);
        }
        {
            var Q0;
            {var subQ0=sQuery(id+"F16.wireOp",EDGE,"E79");Q0=makeQuery(id+"F16.imprint","IMPRINT",FACE,{"disambiguationData":[TD([[makeQuery(id+"F16.imprint","IMPRINT",EDGE,{"derivedFrom":subQ0}),-1.0]])]});}
            var Q1;
            Q1=makeQuery(id+"F16.imprint","IMPRINT",FACE,{"disambiguationData":[TD([[makeQuery(id+"F16.imprint","IMPRINT",EDGE,{"derivedFrom":makeQuery(id+"F1.opExtrude","CAP_EDGE",EDGE,{"disambiguationData":[OSD([sQuery(id+"F0.wireOp",EDGE,"E1.left")])],"isStart":true})}),-1.0]])]});
            var Q2;
            {var subQ1=sQuery(id+"F16.wireOp",EDGE,"E85");Q2=makeQuery(id+"F16.imprint","IMPRINT",FACE,{"disambiguationData":[TD([[makeQuery(id+"F16.imprint","IMPRINT",EDGE,{"derivedFrom":subQ1}),1.0]])]});}
            var Q3;
            Q3=makeQuery(id+"F2.opExtrude","CAP_FACE",FACE,{"disambiguationData":[OSD([sQuery(id+"F0.wireOp",EDGE,"E12"),sQuery(id+"F0.wireOp",EDGE,"E13"),sQuery(id+"F0.wireOp",EDGE,"E14"),sQuery(id+"F0.wireOp",EDGE,"E15"),sQuery(id+"F0.wireOp",EDGE,"E17.filletArc"),sQuery(id+"F0.wireOp",EDGE,"E18.filletArc"),sQuery(id+"F0.wireOp",EDGE,"E19.filletArc"),sQuery(id+"F0.wireOp",EDGE,"E20.filletArc"),sQuery(id+"F0.wireOp",EDGE,"E25.0"),sQuery(id+"F0.wireOp",EDGE,"E25.1"),sQuery(id+"F0.wireOp",EDGE,"E25.2"),sQuery(id+"F0.wireOp",EDGE,"E25.3"),sQuery(id+"F0.wireOp",EDGE,"E25.4"),sQuery(id+"F0.wireOp",EDGE,"E25.5"),sQuery(id+"F0.wireOp",EDGE,"E25.6"),sQuery(id+"F0.wireOp",EDGE,"E25.7")])],"isStart":false});
            extrude(context, id + "F17", {"entities" : qUnion([Q0, Q1, Q2]), "endBound" : BoundingType.UP_TO_SURFACE, "depth" : 25 * mm, "endBoundEntityFace" : qUnion([Q3]), "offsetDistance" : 25 * mm});
        }
    });
